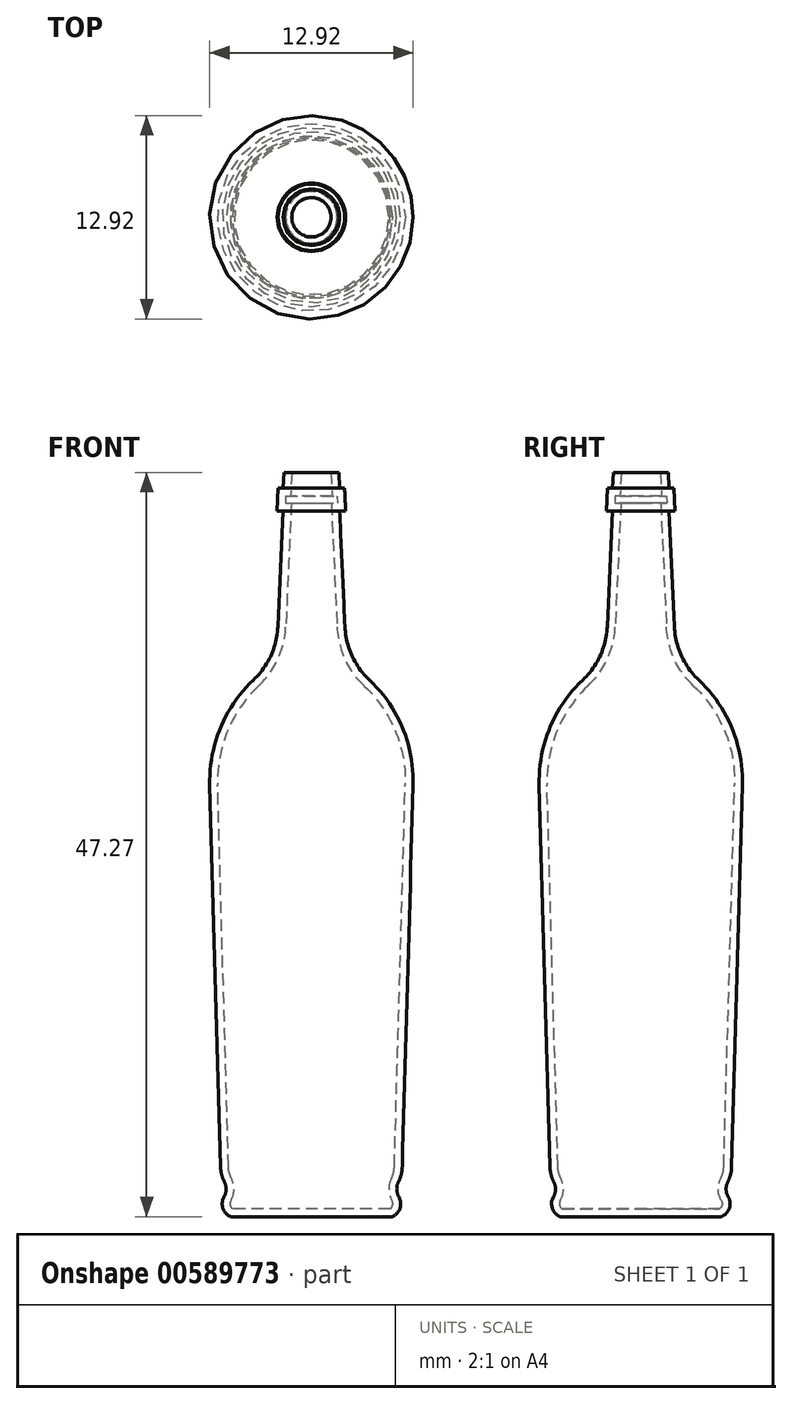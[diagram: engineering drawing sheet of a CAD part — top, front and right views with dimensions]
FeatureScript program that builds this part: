
annotation { "Feature Type Name" : "Feature", "Feature Type Description" : "" }
export const myFeature = defineFeature(function(context is Context, id is Id, definition is map)
    precondition{}
    {
        {
            var Q0;
            Q0=qCreatedBy(makeId("Front.planeOp"),FACE);
            var sketch = newSketch(context, id + "F0", { "sketchPlane" : qUnion([Q0])});
            skLineSegment(sketch, "E0", {"start": v(0, 47.27) * mm, "end": v(0, 0) * mm});
            skLineSegment(sketch, "E1", {"start": v(0, 0) * mm, "end": v(5.12, 0) * mm});
            skLineSegment(sketch, "E2", {"start": v(5.77, 3.18) * mm, "end": v(6.46, 27.4) * mm});
            skArc(sketch, "E3", {"start": v(6.46, 27.4) * mm, "mid": v(5.79, 31.04) * mm, "end": v(3.69, 34.08) * mm});
            skLineSegment(sketch, "E4", {"start": v(1.8, 44.83) * mm, "end": v(2.13, 37.49) * mm});
            skLineSegment(sketch, "E5", {"start": v(2.18, 44.83) * mm, "end": v(2.1, 46.28) * mm});
            skLineSegment(sketch, "E6", {"start": v(1.8, 46.28) * mm, "end": v(2.1, 46.28) * mm});
            skLineSegment(sketch, "E7", {"start": v(1.8, 46.28) * mm, "end": v(1.74, 47.27) * mm});
            skLineSegment(sketch, "E8", {"start": v(0, 47.27) * mm, "end": v(1.74, 47.27) * mm});
            skLineSegment(sketch, "E9", {"start": v(2.18, 44.83) * mm, "end": v(1.8, 44.83) * mm});
            skPoint(sketch, "E10.visualSharp", {"position": v(2.23, 35.2) * mm});
            skArc(sketch, "E10.filletArc", {"start": v(2.13, 37.49) * mm, "mid": v(2.58, 35.64) * mm, "end": v(3.69, 34.08) * mm});
            skArc(sketch, "E11", {"start": v(5.12, 1.64) * mm, "mid": v(5.59, 2.35) * mm, "end": v(5.77, 3.18) * mm});
            skArc(sketch, "E12", {"start": v(5.12, 0) * mm, "mid": v(5.67, 0.82) * mm, "end": v(5.12, 1.64) * mm});
            skSolve(sketch);
        }
        {
            var Q0;
            Q0=makeQuery(id+"F0.imprint","IMPRINT",FACE,{"disambiguationData":[TD([[makeQuery(id+"F0.imprint","IMPRINT",EDGE,{"derivedFrom":sQuery(id+"F0.wireOp",EDGE,"E0")}),1.0]])]});
            var Q1;
            Q1=sQuery(id+"F0.wireOp",EDGE,"E0");
            revolve(context, id + "F1", {"entities" : qUnion([Q0]), "axis" : qUnion([Q1]), "revolveType" : RevolveType.FULL});
        }
        {
            var Q0;
            Q0=makeQuery(id+"F1.opRevolve","SWEPT_EDGE",EDGE,{"disambiguationData":[OSD([sQuery(id+"F0.wireOp",EDGE,"E11"),sQuery(id+"F0.wireOp",EDGE,"E12")])]});
            fillet(context, id + "F2", {"entities" : qUnion([Q0]), "radius" : 1 * mm, "tangentPropagation" : true, "allowEdgeOverflow" : false});
        }
        {
            var Q0;
            Q0=makeQuery(id+"F1.opRevolve","SWEPT_FACE",FACE,{"disambiguationData":[OSD([sQuery(id+"F0.wireOp",EDGE,"E8")])]});
            shell(context, id + "F3", {"entities" : qUnion([Q0]), "thickness" : 0.5 * mm});
        }
    });
